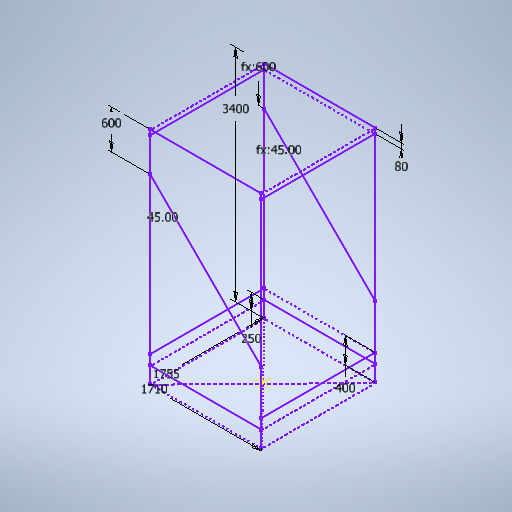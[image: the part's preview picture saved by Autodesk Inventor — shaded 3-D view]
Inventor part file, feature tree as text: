
AUTODESK INVENTOR PART (.ipt)
format: ipt  version: 2025.1 (Build 291241020, 241B)  size: 279,552 bytes
history: native  units: in
note: dims shown in document units (in); Inventor stores cm internally (conversion verified against a paired STEP export)
features: sketch x2
ambient origin geometry x8: Origin, YZ Plane, XZ Plane, XY Plane, X Axis, Y Axis, Z Axis, Center Point
feature tree (2):
  sketch  "Sketch3"  dims[d4=69.0945in d5=67.3228in d7=133.8583in d8=9.8425in d10=23.622in d11=45.0deg d12=45.0deg d13=23.622in d14=15.748in d15=3.1496in]
  sketch  "3D Sketch3"
